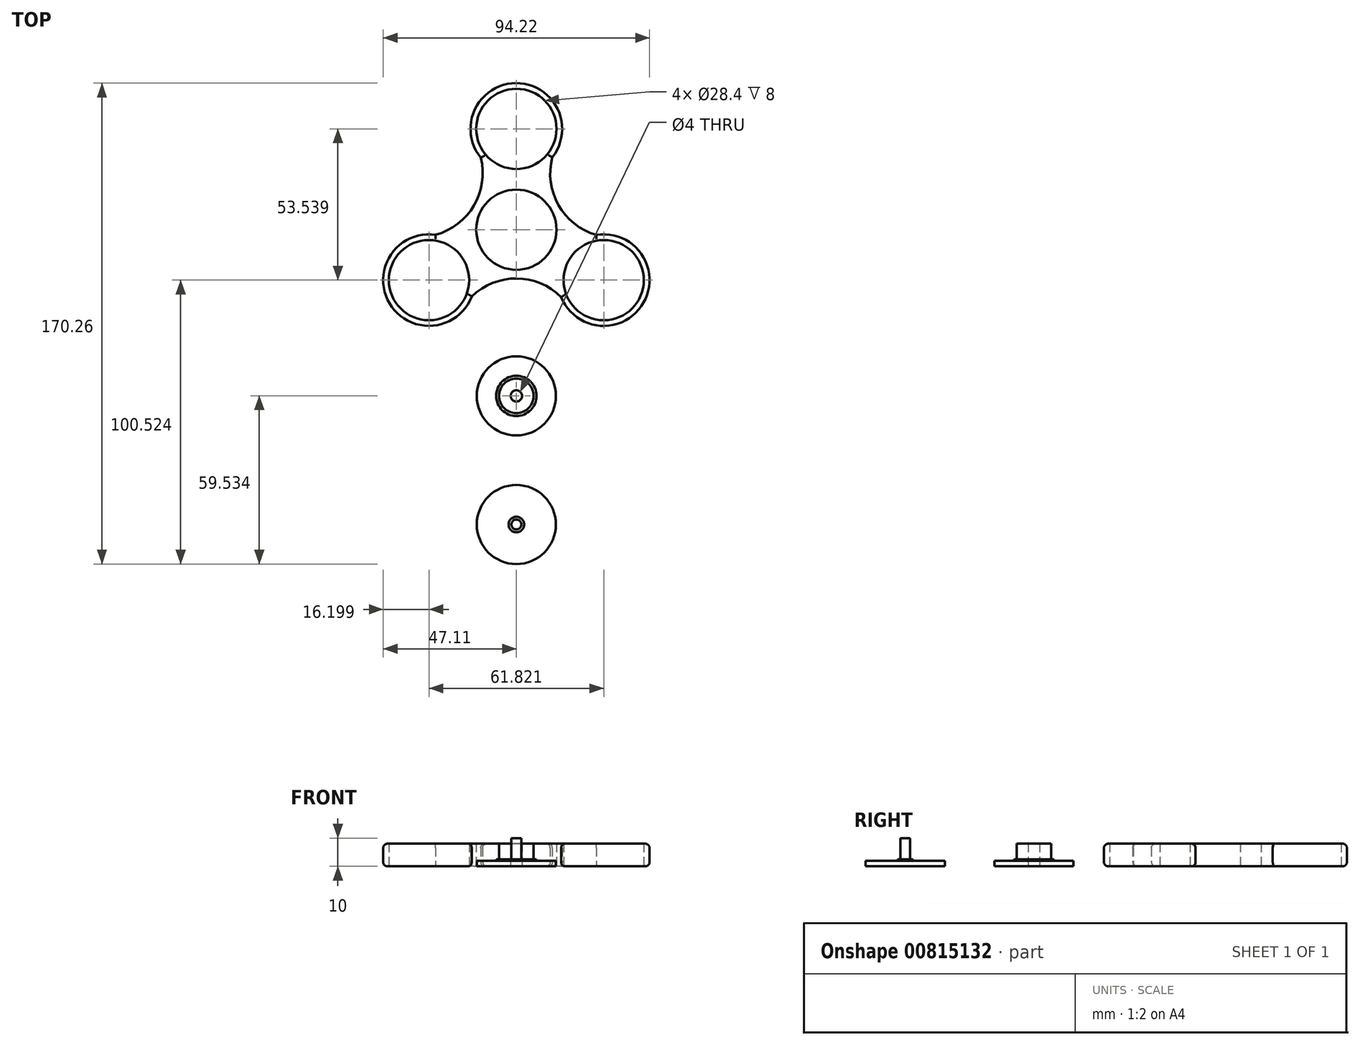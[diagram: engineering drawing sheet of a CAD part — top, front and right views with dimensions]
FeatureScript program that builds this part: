
annotation { "Feature Type Name" : "Feature", "Feature Type Description" : "" }
export const myFeature = defineFeature(function(context is Context, id is Id, definition is map)
    precondition{}
    {
        {
            var Q0;
            Q0=qCreatedBy(makeId("Top.planeOp"),FACE);
            var sketch = newSketch(context, id + "F0", { "sketchPlane" : qUnion([Q0])});
            skCircle(sketch, "E0", {"center": v(0, 0) * mm, "radius": 14.2 * mm});
            skCircle(sketch, "E1", {"center": v(0, 35.7) * mm, "radius": 14.2 * mm});
            skArc(sketch, "E2", {"start": v(12.73, 25.67) * mm, "mid": v(-0.12, 51.9) * mm, "end": v(-12.58, 25.49) * mm});
            skArc(sketch, "E3.1.0", {"start": v(-28.6, -1.81) * mm, "mid": v(-44.88, -26.05) * mm, "end": v(-15.78, -23.64) * mm});
            skCircle(sketch, "E3.1.1", {"center": v(-30.91, -17.85) * mm, "radius": 14.2 * mm});
            skArc(sketch, "E3.2.0", {"start": v(15.87, -23.86) * mm, "mid": v(45, -25.84) * mm, "end": v(28.36, -1.85) * mm});
            skCircle(sketch, "E3.2.1", {"center": v(30.91, -17.85) * mm, "radius": 14.2 * mm});
            skArc(sketch, "E4", {"start": v(15.87, -23.86) * mm, "mid": v(0.09, -17.27) * mm, "end": v(-15.78, -23.64) * mm});
            skArc(sketch, "E5.1.0", {"start": v(12.73, 25.67) * mm, "mid": v(14.9, 8.71) * mm, "end": v(28.36, -1.85) * mm});
            skArc(sketch, "E5.2.0", {"start": v(-28.6, -1.81) * mm, "mid": v(-15, 8.56) * mm, "end": v(-12.58, 25.49) * mm});
            skSolve(sketch);
        }
        {
            var Q0;
            Q0 = qSketchRegion(id + "F0", true);
            extrude(context, id + "F1", {"entities" : qUnion([Q0]), "depth" : 8 * mm, "offsetDistance" : 25 * mm});
        }
        {
            var Q0;
            Q0=makeQuery(id+"F1.opExtrude","CAP_EDGE",EDGE,{"disambiguationData":[OSD([sQuery(id+"F0.wireOp",EDGE,"E3.1.0")])],"isStart":false});
            var Q1;
            Q1=makeQuery(id+"F1.opExtrude","CAP_EDGE",EDGE,{"disambiguationData":[OSD([sQuery(id+"F0.wireOp",EDGE,"E4")])],"isStart":false});
            var Q2;
            Q2=makeQuery(id+"F1.opExtrude","CAP_EDGE",EDGE,{"disambiguationData":[OSD([sQuery(id+"F0.wireOp",EDGE,"E3.2.0")])],"isStart":false});
            var Q3;
            Q3=makeQuery(id+"F1.opExtrude","CAP_EDGE",EDGE,{"disambiguationData":[OSD([sQuery(id+"F0.wireOp",EDGE,"E5.1.0")])],"isStart":false});
            var Q4;
            Q4=makeQuery(id+"F1.opExtrude","CAP_EDGE",EDGE,{"disambiguationData":[OSD([sQuery(id+"F0.wireOp",EDGE,"E2")])],"isStart":false});
            var Q5;
            Q5=makeQuery(id+"F1.opExtrude","CAP_EDGE",EDGE,{"disambiguationData":[OSD([sQuery(id+"F0.wireOp",EDGE,"E5.2.0")])],"isStart":false});
            var Q6;
            Q6=makeQuery(id+"F1.opExtrude","CAP_EDGE",EDGE,{"disambiguationData":[OSD([sQuery(id+"F0.wireOp",EDGE,"E4")])],"isStart":true});
            var Q7;
            Q7=makeQuery(id+"F1.opExtrude","CAP_EDGE",EDGE,{"disambiguationData":[OSD([sQuery(id+"F0.wireOp",EDGE,"E3.1.0")])],"isStart":true});
            var Q8;
            Q8=makeQuery(id+"F1.opExtrude","CAP_EDGE",EDGE,{"disambiguationData":[OSD([sQuery(id+"F0.wireOp",EDGE,"E5.2.0")])],"isStart":true});
            var Q9;
            Q9=makeQuery(id+"F1.opExtrude","CAP_EDGE",EDGE,{"disambiguationData":[OSD([sQuery(id+"F0.wireOp",EDGE,"E2")])],"isStart":true});
            var Q10;
            Q10=makeQuery(id+"F1.opExtrude","CAP_EDGE",EDGE,{"disambiguationData":[OSD([sQuery(id+"F0.wireOp",EDGE,"E5.1.0")])],"isStart":true});
            var Q11;
            Q11=makeQuery(id+"F1.opExtrude","CAP_EDGE",EDGE,{"disambiguationData":[OSD([sQuery(id+"F0.wireOp",EDGE,"E3.2.0")])],"isStart":true});
            fillet(context, id + "F2", {"entities" : qUnion([Q0, Q1, Q2, Q3, Q4, Q5, Q6, Q7, Q8, Q9, Q10, Q11]), "radius" : 1.5 * mm, "tangentPropagation" : true, "allowEdgeOverflow" : false});
        }
        {
            var Q0;
            Q0=qCreatedBy(makeId("Right.planeOp"),FACE);
            var sketch = newSketch(context, id + "F3", { "sketchPlane" : qUnion([Q0])});
            skLineSegment(sketch, "E6", {"start": v(-72.84, 0) * mm, "end": v(-72.84, 2) * mm});
            skLineSegment(sketch, "E7", {"start": v(-72.84, 2) * mm, "end": v(-65.95, 2) * mm});
            skLineSegment(sketch, "E8", {"start": v(-58.84, 0) * mm, "end": v(-72.84, 0) * mm});
            skLineSegment(sketch, "E9.top", {"start": v(-64.95, 8) * mm, "end": v(-58.84, 8) * mm});
            skLineSegment(sketch, "E9.left", {"start": v(-64.95, 2.5) * mm, "end": v(-64.95, 8) * mm});
            skPoint(sketch, "E10.start.orphan", {"position": v(-58.84, 0) * mm});
            skLineSegment(sketch, "E11.top", {"start": v(-64.95, 2.5) * mm, "end": v(-65.95, 2.5) * mm});
            skLineSegment(sketch, "E11.right", {"start": v(-65.95, 2) * mm, "end": v(-65.95, 2.5) * mm});
            skLineSegment(sketch, "E12", {"start": v(-58.84, 8) * mm, "end": v(-58.84, 0) * mm});
            skSolve(sketch);
        }
        {
            var Q0;
            Q0=makeQuery(id+"F3.imprint","IMPRINT",FACE,{"disambiguationData":[TD([[makeQuery(id+"F3.imprint","IMPRINT",EDGE,{"derivedFrom":sQuery(id+"F3.wireOp",EDGE,"E6")}),-1.0]])]});
            var Q1;
            Q1=sQuery(id+"F3.wireOp",EDGE,"E12");
            revolve(context, id + "F4", {"surfaceOperationType" : NewSurfaceOperationType.NEW, "entities" : qUnion([Q0]), "axis" : qUnion([Q1]), "revolveType" : RevolveType.FULL});
        }
        {
            var Q0;
            Q0=makeQuery(id+"F4.opRevolve","SWEPT_FACE",FACE,{"disambiguationData":[OSD([sQuery(id+"F3.wireOp",EDGE,"E8")])]});
            var sketch = newSketch(context, id + "F5", { "sketchPlane" : qUnion([Q0])});
            skPoint(sketch, "E13", {"position": v(0, 58.84) * mm});
            skSolve(sketch);
        }
        {
            var Q0;
            Q0=sQuery(id+"F5.wireOp",VERTEX,"E13");
            var Q1;
            Q1=makeQuery(id+"F4.opRevolve","SWEPT_BODY",BODY,{"disambiguationData":[OSD([sQuery(id+"F3.wireOp",EDGE,"E6"),sQuery(id+"F3.wireOp",EDGE,"E7"),sQuery(id+"F3.wireOp",EDGE,"E8"),sQuery(id+"F3.wireOp",EDGE,"E9.top"),sQuery(id+"F3.wireOp",EDGE,"E9.left"),sQuery(id+"F3.wireOp",EDGE,"E11.top"),sQuery(id+"F3.wireOp",EDGE,"E11.right"),sQuery(id+"F3.wireOp",EDGE,"E12")])]});
            hole(context, id + "F6", {"style" : HoleStyle.SIMPLE, "endStyle" : HoleEndStyle.THROUGH, "holeDiameter" : 4 * mm, "majorDiameter" : 5 * mm, "isTappedThrough" : true, "tappedDepth" : 12 * mm, "tapClearance" : 3, "startFromSketch" : true, "locations" : qUnion([Q0]), "scope" : qUnion([Q1])});
        }
        {
            var Q0;
            Q0=qCreatedBy(makeId("Right.planeOp"),FACE);
            var sketch = newSketch(context, id + "F7", { "sketchPlane" : qUnion([Q0])});
            skLineSegment(sketch, "E14", {"start": v(-118.37, 0) * mm, "end": v(-104.37, 0) * mm});
            skLineSegment(sketch, "E15", {"start": v(-104.37, 0) * mm, "end": v(-104.37, 10) * mm});
            skLineSegment(sketch, "E16", {"start": v(-104.37, 10) * mm, "end": v(-106.12, 10) * mm});
            skLineSegment(sketch, "E17", {"start": v(-106.12, 10) * mm, "end": v(-106.12, 2.5) * mm});
            skLineSegment(sketch, "E18", {"start": v(-106.12, 2.5) * mm, "end": v(-107.12, 2.5) * mm});
            skLineSegment(sketch, "E19", {"start": v(-107.12, 2.5) * mm, "end": v(-107.12, 2) * mm});
            skLineSegment(sketch, "E20", {"start": v(-118.37, 0) * mm, "end": v(-118.37, 2) * mm});
            skLineSegment(sketch, "E21", {"start": v(-118.37, 2) * mm, "end": v(-107.12, 2) * mm});
            skSolve(sketch);
        }
        {
            var Q0;
            Q0 = qSketchRegion(id + "F7", true);
            var Q1;
            Q1=sQuery(id+"F7.wireOp",EDGE,"E15");
            revolve(context, id + "F8", {"surfaceOperationType" : NewSurfaceOperationType.NEW, "entities" : qUnion([Q0]), "axis" : qUnion([Q1]), "revolveType" : RevolveType.FULL});
        }
    });
